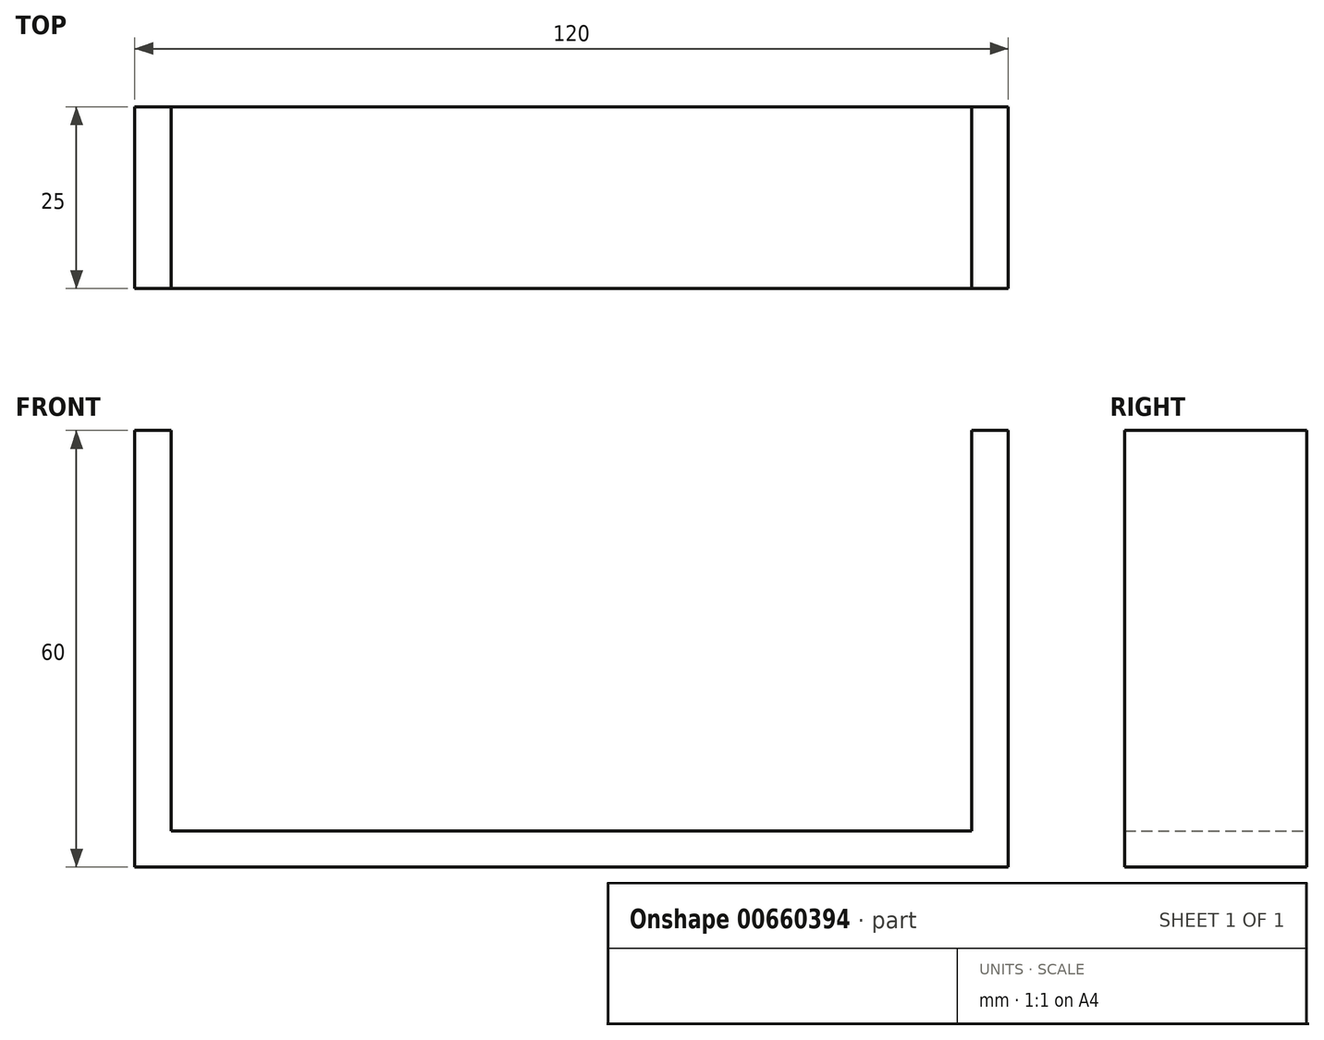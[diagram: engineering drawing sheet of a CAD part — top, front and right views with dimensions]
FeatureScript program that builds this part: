
annotation { "Feature Type Name" : "Feature", "Feature Type Description" : "" }
export const myFeature = defineFeature(function(context is Context, id is Id, definition is map)
    precondition{}
    {
        {
            var Q0;
            Q0=qCreatedBy(makeId("Front.planeOp"),FACE);
            var sketch = newSketch(context, id + "F0", { "sketchPlane" : qUnion([Q0])});
            skLineSegment(sketch, "E0", {"start": v(0, 0) * mm, "end": v(0, -55) * mm});
            skLineSegment(sketch, "E1", {"start": v(0, -55) * mm, "end": v(110, -55) * mm});
            skLineSegment(sketch, "E2", {"start": v(110, -55) * mm, "end": v(110, 0) * mm});
            skLineSegment(sketch, "E3.0", {"start": v(115, -60) * mm, "end": v(115, 0) * mm});
            skLineSegment(sketch, "E3.1", {"start": v(-5, -60) * mm, "end": v(115, -60) * mm});
            skLineSegment(sketch, "E3.2", {"start": v(-5, 0) * mm, "end": v(-5, -60) * mm});
            skLineSegment(sketch, "E4", {"start": v(-5, 0) * mm, "end": v(0, 0) * mm});
            skLineSegment(sketch, "E5", {"start": v(110, 0) * mm, "end": v(115, 0) * mm});
            skSolve(sketch);
        }
        {
            var Q0;
            Q0=makeQuery(id+"F0.imprint","IMPRINT",FACE,{"disambiguationData":[TD([[makeQuery(id+"F0.imprint","IMPRINT",EDGE,{"derivedFrom":sQuery(id+"F0.wireOp",EDGE,"E0")}),-1.0]])]});
            extrude(context, id + "F1", {"entities" : qUnion([Q0]), "depth" : 25 * mm, "offsetDistance" : 25 * mm});
        }
    });
